# Revit family: v-584h4_50Hz
name_source: partatom
category: 機械設備
units: mm (PartAtom-declared; Revit-internal decimal feet)

## family parameters
OmniClass タイトル = Centrifugal Fans
OmniClass 番号 = 23.75.35.17.27
パーツ タイプ = 標準
ロード時にボイドで切り取り = いいえ
丸型コネクタ寸法 = 直径を使用
作業面ベース = いいえ
共有 = いいえ
常に垂直 = はい
部屋計算ポイント = いいえ

## types (1)
- V-584H4
    Clearance Back = 0  [stored 0 ft]
    Clearance Bottom = 0  [stored 0 ft]
    Clearance Front = 0  [stored 0 ft]
    Clearance Left = 0  [stored 0 ft]
    Clearance Right = 0  [stored 0 ft]
    Clearance Top = 0  [stored 0 ft]
    D1 = 495  [stored 1.62402 ft]
    D2 = 345  [stored 1.13189 ft]
    Depth = 597
    Duct_D = 150
    Duct_Height = 56  [stored 0.183727 ft]
    EAサイズ_D = 148  [stored 0.485564 ft]
    H1 = 600
    Height = 325  [stored 1.06627 ft]
    IfcExportAs = IfcFanType
    IfcExportType = CENTRIFUGALFORWARDCURVED
    MAX静圧 = 0.0 Pa
    MAX風量 = 710.0 m³/h
    MID静圧 = 0.0 Pa
    MID風量 = 0.0 m³/h
    MIN静圧 = 0.0 Pa
    MIN風量 = 370.0 m³/h
    OmniClassCode = 23-33 31 19 13 15
    URL = https://www.mitsubishielectric.co.jp
    Uniclass2015Code = Pr_65_67_29_12
    Uniclass2015Title = Centrifugal fans
    Uniclass2015Version = Systems v1.9
    W1 = 290  [stored 0.951444 ft]
    Width = 580  [stored 1.90289 ft]
    ☑給気／□排気 = いいえ
    ダクト径 = 150 mm
    マテリアル = 鋼板(シルバー)
    モデル = V-584H4
    仕様書バージョン = Version1.0
    企業コード = 108420
    価格 = 0 $
    分類コード = 50052503100060
    周波数 = 50 Hz
    呼称 = 遠心送風機
    外気量 = 0.0 m³/h
    天吊用穴_D_右・左配管 = 290  [stored 0.951444 ft]
    天吊用穴_D_後・上配管 = 255  [stored 0.836614 ft]
    天吊用穴_ピッチ = 480  [stored 1.5748 ft]
    実風量 = 0.0 m³/h
    形式 = 片吸込形
    排気量 = 0.0 m³/h
    極数 = 2
    機外静圧 = 0.0 Pa
    機外静圧_排気 = 210.0 Pa
    法定耐用年数 = 15
    消費電力 = 132 W
    相 = 1
    積算_科目 = 2 換気設備
    符号 = FE
    製品リリース年月 = 2022年6月1日
    製品出荷対象 = 国内
    製品質量 = 20.00 kg
    製造元 = 三菱電機株式会社
    設置方法 = 天吊
    設計風量 = 0.0 m³/h
    説明 = レンジフードファン 深形 58cm幅タイプ(取替対応)
    負荷分類 = 3_ファン類
    質量 = 24.00 kg
    運転質量 = 0.00 kg
    電動機出力 = 0 W
    電圧 = 100 V
    風量 = 710.0 m³/h
    騒音レベル(dB(A)) = 48

note: [stored X ft] marks values corroborated as IEEE doubles in the binary element streams (Revit-internal decimal feet)

## geometry (parser evidence)
native form markers: Blend x2
no freeform markers — native parametric forms only
